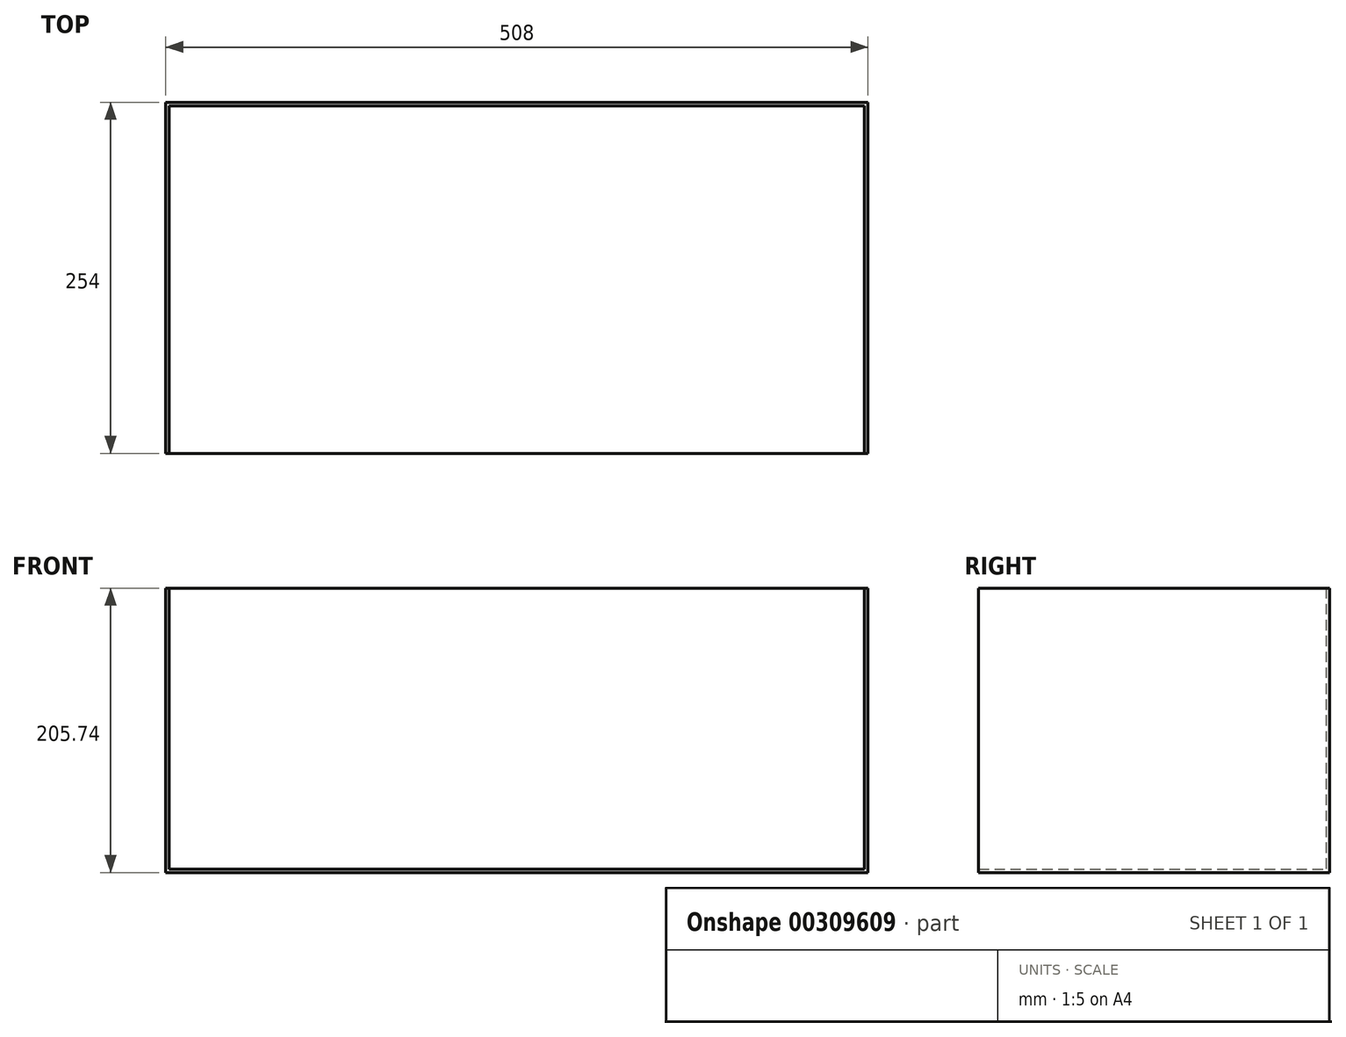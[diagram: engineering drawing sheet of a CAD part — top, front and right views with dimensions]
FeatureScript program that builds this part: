
annotation { "Feature Type Name" : "Feature", "Feature Type Description" : "" }
export const myFeature = defineFeature(function(context is Context, id is Id, definition is map)
    precondition{}
    {
        {
            var Q0;
            Q0=qCreatedBy(makeId("Top.planeOp"),FACE);
            var sketch = newSketch(context, id + "F0", { "sketchPlane" : qUnion([Q0])});
            skLineSegment(sketch, "E0.bottom", {"start": v(254, -127) * mm, "end": v(-254, -127) * mm});
            skLineSegment(sketch, "E0.top", {"start": v(254, 127) * mm, "end": v(-254, 127) * mm});
            skLineSegment(sketch, "E0.left", {"start": v(254, -127) * mm, "end": v(254, 127) * mm});
            skLineSegment(sketch, "E0.right", {"start": v(-254, -127) * mm, "end": v(-254, 127) * mm});
            skPoint(sketch, "E0.middle", {"position": v(0, 0) * mm});
            skSolve(sketch);
        }
        {
            var Q0;
            Q0 = qSketchRegion(id + "F0", true);
            extrude(context, id + "F1", {"entities" : qUnion([Q0]), "depth" : 2.54 * mm});
        }
        {
            var Q0;
            Q0=makeQuery(id+"F1.opExtrude","CAP_FACE",FACE,{"disambiguationData":[OSD([sQuery(id+"F0.wireOp",EDGE,"E0.bottom"),sQuery(id+"F0.wireOp",EDGE,"E0.top"),sQuery(id+"F0.wireOp",EDGE,"E0.left"),sQuery(id+"F0.wireOp",EDGE,"E0.right")])],"isStart":false});
            var sketch = newSketch(context, id + "F2", { "sketchPlane" : qUnion([Q0])});
            skLineSegment(sketch, "E1.bottom", {"start": v(-254, 127) * mm, "end": v(-251.46, 127) * mm});
            skLineSegment(sketch, "E1.top", {"start": v(-254, -127) * mm, "end": v(-251.46, -127) * mm});
            skLineSegment(sketch, "E1.left", {"start": v(-254, 127) * mm, "end": v(-254, -127) * mm});
            skLineSegment(sketch, "E1.right", {"start": v(-251.46, 127) * mm, "end": v(-251.46, -127) * mm});
            skSolve(sketch);
        }
        {
            var Q0;
            Q0 = qSketchRegion(id + "F2", true);
            extrude(context, id + "F3", {"entities" : qUnion([Q0]), "operationType" : NewBodyOperationType.ADD, "depth" : 203.2 * mm});
        }
        {
            var Q0;
            Q0=makeQuery(id+"F1.opExtrude","CAP_FACE",FACE,{"disambiguationData":[OSD([sQuery(id+"F0.wireOp",EDGE,"E0.bottom"),sQuery(id+"F0.wireOp",EDGE,"E0.top"),sQuery(id+"F0.wireOp",EDGE,"E0.left"),sQuery(id+"F0.wireOp",EDGE,"E0.right")])],"isStart":false});
            var sketch = newSketch(context, id + "F4", { "sketchPlane" : qUnion([Q0])});
            skLineSegment(sketch, "E2.bottom", {"start": v(254, 127) * mm, "end": v(-251.46, 127) * mm});
            skLineSegment(sketch, "E2.top", {"start": v(254, 124.46) * mm, "end": v(-251.46, 124.46) * mm});
            skLineSegment(sketch, "E2.left", {"start": v(254, 127) * mm, "end": v(254, 124.46) * mm});
            skLineSegment(sketch, "E2.right", {"start": v(-251.46, 127) * mm, "end": v(-251.46, 124.46) * mm});
            skLineSegment(sketch, "E3.top", {"start": v(-251.46, 127) * mm, "end": v(-49.61, 127) * mm});
            skSolve(sketch);
        }
        {
            var Q0;
            {var subQ0=sQuery(id+"F4.wireOp",EDGE,"E2.right");Q0=makeQuery(id+"F4.imprint","IMPRINT",FACE,{"disambiguationData":[TD([[makeQuery(id+"F4.imprint","IMPRINT",EDGE,{"derivedFrom":subQ0}),1.0]])]});}
            extrude(context, id + "F5", {"entities" : qUnion([Q0]), "operationType" : NewBodyOperationType.ADD, "depth" : 203.2 * mm});
        }
        {
            var Q0;
            Q0=makeQuery(id+"F1.opExtrude","CAP_FACE",FACE,{"disambiguationData":[OSD([sQuery(id+"F0.wireOp",EDGE,"E0.bottom"),sQuery(id+"F0.wireOp",EDGE,"E0.top"),sQuery(id+"F0.wireOp",EDGE,"E0.left"),sQuery(id+"F0.wireOp",EDGE,"E0.right")])],"isStart":false});
            var sketch = newSketch(context, id + "F6", { "sketchPlane" : qUnion([Q0])});
            skLineSegment(sketch, "E4.bottom", {"start": v(254, -127) * mm, "end": v(251.46, -127) * mm});
            skLineSegment(sketch, "E4.top", {"start": v(254, 124.46) * mm, "end": v(251.46, 124.46) * mm});
            skLineSegment(sketch, "E4.left", {"start": v(254, -127) * mm, "end": v(254, 124.46) * mm});
            skLineSegment(sketch, "E4.right", {"start": v(251.46, -127) * mm, "end": v(251.46, 124.46) * mm});
            skSolve(sketch);
        }
        {
            var Q0;
            Q0=makeQuery(id+"F6.imprint","IMPRINT",FACE,{"disambiguationData":[TD([[makeQuery(id+"F6.imprint","IMPRINT",EDGE,{"derivedFrom":sQuery(id+"F6.wireOp",EDGE,"E4.bottom")}),-1.0]])]});
            extrude(context, id + "F7", {"entities" : qUnion([Q0]), "operationType" : NewBodyOperationType.ADD, "depth" : 203.2 * mm});
        }
    });
